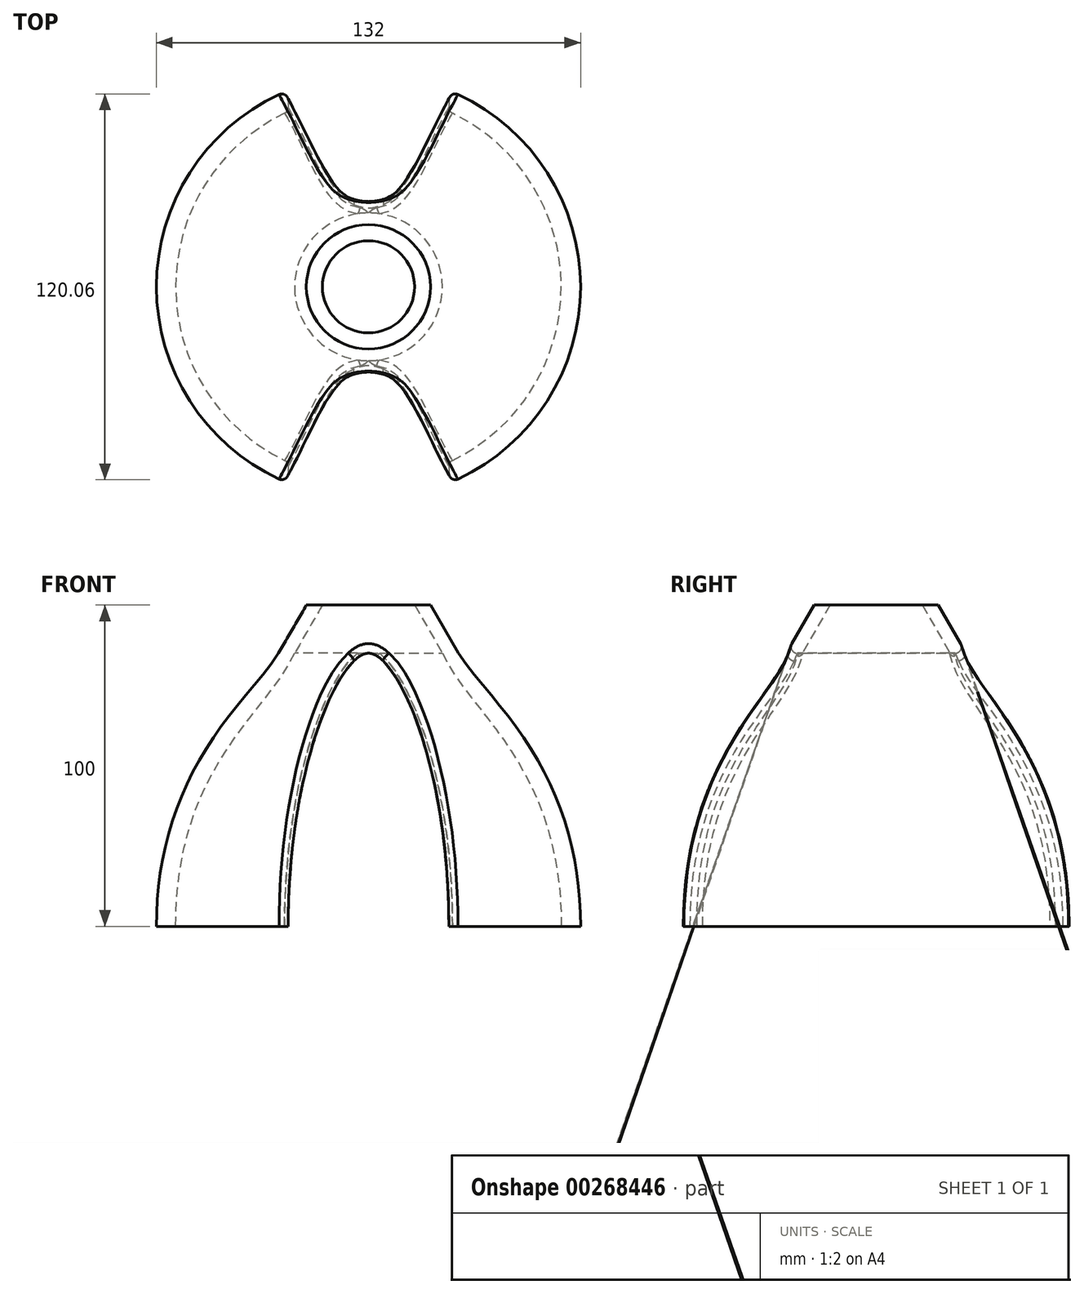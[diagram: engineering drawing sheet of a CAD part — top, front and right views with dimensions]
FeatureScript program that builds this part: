
annotation { "Feature Type Name" : "Feature", "Feature Type Description" : "" }
export const myFeature = defineFeature(function(context is Context, id is Id, definition is map)
    precondition{}
    {
        {
            var Q0;
            Q0=qCreatedBy(makeId("Front.planeOp"),FACE);
            var sketch = newSketch(context, id + "F0", { "sketchPlane" : qUnion([Q0])});
            skLineSegment(sketch, "E0", {"start": v(-14.34, 15) * mm, "end": v(-19.34, 15) * mm});
            skLineSegment(sketch, "E1", {"start": v(-19.34, 15) * mm, "end": v(-28, 0) * mm});
            skLineSegment(sketch, "E2", {"start": v(-28, 0) * mm, "end": v(-23, 0) * mm});
            skLineSegment(sketch, "E3.bottom", {"start": v(0, 0) * mm, "end": v(44.52, 0) * mm, "construction": true});
            skLineSegment(sketch, "E3.top", {"start": v(0, 38.4) * mm, "end": v(44.52, 38.4) * mm, "construction": true});
            skLineSegment(sketch, "E3.left", {"start": v(0, 0) * mm, "end": v(0, 38.4) * mm, "construction": true});
            skLineSegment(sketch, "E3.right", {"start": v(44.52, 0) * mm, "end": v(44.52, 38.4) * mm, "construction": true});
            skLineSegment(sketch, "E4", {"start": v(-14.34, 15) * mm, "end": v(-23, 0) * mm});
            skSolve(sketch);
        }
        {
            var Q0;
            Q0=makeQuery(id+"F0.imprint","IMPRINT",FACE,{"disambiguationData":[TD([[makeQuery(id+"F0.imprint","IMPRINT",EDGE,{"derivedFrom":sQuery(id+"F0.wireOp",EDGE,"E0")}),1.0]])]});
            var Q1;
            Q1=sQuery(id+"F0.wireOp",EDGE,"E3.left");
            revolve(context, id + "F1", {"surfaceOperationType" : NewSurfaceOperationType.NEW, "entities" : qUnion([Q0]), "axis" : qUnion([Q1]), "revolveType" : RevolveType.FULL});
        }
        {
            var Q0;
            Q0=qCreatedBy(makeId("Front.planeOp"),FACE);
            var sketch = newSketch(context, id + "F2", { "sketchPlane" : qUnion([Q0])});
            skLineSegment(sketch, "E5", {"start": v(-28, 0) * mm, "end": v(-19.38, 14.93) * mm, "construction": true});
            skFitSpline(sketch, "E6", {"points": [v(-28, 0) * mm, v(-66, -85) * mm], "startDerivative": vector(-22.5, -38.97) * mm, "endDerivative": vector(0, -150) * mm});
            skLineSegment(sketch, "E7", {"start": v(-66, -85) * mm, "end": v(-60, -85) * mm});
            skLineSegment(sketch, "E8.0", {"start": v(23, 0) * mm, "end": v(-23, 0) * mm, "construction": true});
            skFitSpline(sketch, "E9", {"points": [v(-60, -85) * mm, v(-23, 0) * mm], "startDerivative": vector(0, 150) * mm, "endDerivative": vector(25.12, 56.33) * mm});
            skLineSegment(sketch, "E10.0", {"start": v(14.34, 15) * mm, "end": v(-14.34, 15) * mm, "construction": true});
            skLineSegment(sketch, "E11", {"start": v(-14.34, 15) * mm, "end": v(-23, 0) * mm, "construction": true});
            skLineSegment(sketch, "E12", {"start": v(-28, 0) * mm, "end": v(-23, 0) * mm});
            skLineSegment(sketch, "E13", {"start": v(0, 0) * mm, "end": v(0, -38.45) * mm, "construction": true});
            skSolve(sketch);
        }
        {
            var Q0;
            Q0=makeQuery(id+"F2.imprint","IMPRINT",FACE,{"disambiguationData":[TD([[makeQuery(id+"F2.imprint","IMPRINT",EDGE,{"derivedFrom":sQuery(id+"F2.wireOp",EDGE,"E6")}),1.0]])]});
            var Q1;
            Q1=sQuery(id+"F2.wireOp",EDGE,"E13");
            revolve(context, id + "F3", {"operationType" : NewBodyOperationType.ADD, "surfaceOperationType" : NewSurfaceOperationType.NEW, "entities" : qUnion([Q0]), "axis" : qUnion([Q1]), "revolveType" : RevolveType.FULL});
        }
        {
            var Q0;
            Q0=qCreatedBy(makeId("Front.planeOp"),FACE);
            var sketch = newSketch(context, id + "F4", { "sketchPlane" : qUnion([Q0])});
            skLineSegment(sketch, "E14.0", {"start": v(-66, -85) * mm, "end": v(66, -85) * mm});
            skLineSegment(sketch, "E15", {"start": v(0, 0) * mm, "end": v(0, -85) * mm, "construction": true});
            skFitSpline(sketch, "E16", {"points": [v(0, 0) * mm, v(-25, -85) * mm], "startDerivative": vector(-26.97, 0) * mm, "endDerivative": vector(0, -150) * mm});
            skLineSegment(sketch, "E17", {"start": v(0, 0) * mm, "end": v(-8.99, 0) * mm, "construction": true});
            skFitSpline(sketch, "E18.MirrorCS", {"points": [v(0, 0) * mm, v(25, -85) * mm], "startDerivative": vector(26.97, 0) * mm, "endDerivative": vector(0, -150) * mm});
            skSolve(sketch);
        }
        {
            var Q0;
            {var subQ0=sQuery(id+"F4.wireOp",EDGE,"E16");Q0=makeQuery(id+"F4.imprint","IMPRINT",FACE,{"disambiguationData":[TD([[makeQuery(id+"F4.imprint","IMPRINT",EDGE,{"derivedFrom":subQ0}),1.0]])]});}
            extrude(context, id + "F5", {"entities" : qUnion([Q0]), "operationType" : NewBodyOperationType.REMOVE, "oppositeDirection" : true, "depth" : 200 * mm, "offsetDistance" : 25 * mm, "symmetric" : true});
        }
        {
            var Q0;
            Q0=makeQuery(id+"F5.boolean.opBoolean","INTERSECT",EDGE,{"disambiguationData":[OD(0.0)],"derivedFrom":[makeQuery(id+"F3.opRevolve","SWEPT_FACE",FACE,{"disambiguationData":[OSD([sQuery(id+"F2.wireOp",EDGE,"E6")])]}),makeQuery(id+"F5.opExtrude","SWEPT_FACE",FACE,{"disambiguationData":[OSD([sQuery(id+"F4.wireOp",EDGE,"E16")])]})]});
            var Q1;
            Q1=makeQuery(id+"F5.boolean.opBoolean","INTERSECT",EDGE,{"disambiguationData":[OD(0.0)],"derivedFrom":[makeQuery(id+"F3.opRevolve","SWEPT_FACE",FACE,{"disambiguationData":[OSD([sQuery(id+"F2.wireOp",EDGE,"E6")])]}),makeQuery(id+"F5.opExtrude","SWEPT_FACE",FACE,{"disambiguationData":[OSD([sQuery(id+"F4.wireOp",EDGE,"E18.MirrorCS")])]})]});
            var Q2;
            Q2=makeQuery(id+"FsHivhGLS4HPiXr_1.1.F5.boolean.opBoolean","INTERSECT",EDGE,{"derivedFrom":[makeQuery(id+"F5.boolean.opBoolean","SPLIT",FACE,{"disambiguationData":[OD(1.0)],"derivedFrom":makeQuery(id+"F3.opRevolve","SWEPT_FACE",FACE,{"disambiguationData":[OSD([sQuery(id+"F2.wireOp",EDGE,"E6")])]})}),makeQuery(id+"FsHivhGLS4HPiXr_1.1.F5.opExtrude","SWEPT_FACE",FACE,{"disambiguationData":[OSD([sQuery(id+"F4.wireOp",EDGE,"E16")])]})]});
            var Q3;
            Q3=makeQuery(id+"FsHivhGLS4HPiXr_1.1.F5.boolean.opBoolean","INTERSECT",EDGE,{"derivedFrom":[makeQuery(id+"F5.boolean.opBoolean","SPLIT",FACE,{"disambiguationData":[OD(1.0)],"derivedFrom":makeQuery(id+"F3.opRevolve","SWEPT_FACE",FACE,{"disambiguationData":[OSD([sQuery(id+"F2.wireOp",EDGE,"E6")])]})}),makeQuery(id+"FsHivhGLS4HPiXr_1.1.F5.opExtrude","SWEPT_FACE",FACE,{"disambiguationData":[OSD([sQuery(id+"F4.wireOp",EDGE,"E18.MirrorCS")])]})]});
            var Q4;
            {var subQ0=sQuery(id+"F4.wireOp",EDGE,"E16");var subQ1=makeQuery(id+"F3.opRevolve","SWEPT_FACE",FACE,{"disambiguationData":[OSD([sQuery(id+"F2.wireOp",EDGE,"E6")])]});Q4=makeQuery(id+"FsHivhGLS4HPiXr_1.2.F5.boolean.opBoolean","INTERSECT",EDGE,{"derivedFrom":[makeQuery(id+"FsHivhGLS4HPiXr_1.1.F5.boolean.opBoolean","SPLIT",FACE,{"disambiguationData":[TD([makeQuery(id+"F5.boolean.opBoolean","COPY",FACE,{"disambiguationData":[OD(1.0)],"derivedFrom":makeQuery(id+"F5.opExtrude","SWEPT_FACE",FACE,{"disambiguationData":[OSD([subQ0])]})})])],"derivedFrom":makeQuery(id+"F5.boolean.opBoolean","SPLIT",FACE,{"disambiguationData":[OD(1.0)],"derivedFrom":subQ1})}),makeQuery(id+"FsHivhGLS4HPiXr_1.2.F5.opExtrude","SWEPT_FACE",FACE,{"disambiguationData":[OSD([subQ0])]})]});}
            var Q5;
            Q5=makeQuery(id+"F5.boolean.opBoolean","INTERSECT",EDGE,{"disambiguationData":[OD(1.0)],"derivedFrom":[makeQuery(id+"F3.opRevolve","SWEPT_FACE",FACE,{"disambiguationData":[OSD([sQuery(id+"F2.wireOp",EDGE,"E6")])]}),makeQuery(id+"F5.opExtrude","SWEPT_FACE",FACE,{"disambiguationData":[OSD([sQuery(id+"F4.wireOp",EDGE,"E18.MirrorCS")])]})]});
            var Q6;
            Q6=makeQuery(id+"F5.boolean.opBoolean","INTERSECT",EDGE,{"disambiguationData":[OD(1.0)],"derivedFrom":[makeQuery(id+"F3.opRevolve","SWEPT_FACE",FACE,{"disambiguationData":[OSD([sQuery(id+"F2.wireOp",EDGE,"E6")])]}),makeQuery(id+"F5.opExtrude","SWEPT_FACE",FACE,{"disambiguationData":[OSD([sQuery(id+"F4.wireOp",EDGE,"E16")])]})]});
            var Q7;
            Q7=makeQuery(id+"FsHivhGLS4HPiXr_1.1.F5.boolean.opBoolean","INTERSECT",EDGE,{"derivedFrom":[makeQuery(id+"F5.boolean.opBoolean","SPLIT",FACE,{"disambiguationData":[OD(0.0)],"derivedFrom":makeQuery(id+"F3.opRevolve","SWEPT_FACE",FACE,{"disambiguationData":[OSD([sQuery(id+"F2.wireOp",EDGE,"E6")])]})}),makeQuery(id+"FsHivhGLS4HPiXr_1.1.F5.opExtrude","SWEPT_FACE",FACE,{"disambiguationData":[OSD([sQuery(id+"F4.wireOp",EDGE,"E16")])]})]});
            var Q8;
            Q8=makeQuery(id+"FsHivhGLS4HPiXr_1.1.F5.boolean.opBoolean","INTERSECT",EDGE,{"derivedFrom":[makeQuery(id+"F5.boolean.opBoolean","SPLIT",FACE,{"disambiguationData":[OD(0.0)],"derivedFrom":makeQuery(id+"F3.opRevolve","SWEPT_FACE",FACE,{"disambiguationData":[OSD([sQuery(id+"F2.wireOp",EDGE,"E6")])]})}),makeQuery(id+"FsHivhGLS4HPiXr_1.1.F5.opExtrude","SWEPT_FACE",FACE,{"disambiguationData":[OSD([sQuery(id+"F4.wireOp",EDGE,"E18.MirrorCS")])]})]});
            var Q9;
            {var subQ0=sQuery(id+"F4.wireOp",EDGE,"E18.MirrorCS");var subQ1=sQuery(id+"F4.wireOp",EDGE,"E16");var subQ2=makeQuery(id+"F3.opRevolve","SWEPT_FACE",FACE,{"disambiguationData":[OSD([sQuery(id+"F2.wireOp",EDGE,"E6")])]});Q9=makeQuery(id+"FsHivhGLS4HPiXr_1.2.F5.boolean.opBoolean","INTERSECT",EDGE,{"derivedFrom":[makeQuery(id+"FsHivhGLS4HPiXr_1.1.F5.boolean.opBoolean","SPLIT",FACE,{"disambiguationData":[TD([makeQuery(id+"F5.boolean.opBoolean","COPY",FACE,{"disambiguationData":[OD(0.0)],"derivedFrom":makeQuery(id+"F5.opExtrude","SWEPT_FACE",FACE,{"disambiguationData":[OSD([subQ1])]})})])],"derivedFrom":makeQuery(id+"F5.boolean.opBoolean","SPLIT",FACE,{"disambiguationData":[OD(0.0)],"derivedFrom":subQ2})}),makeQuery(id+"FsHivhGLS4HPiXr_1.2.F5.opExtrude","SWEPT_FACE",FACE,{"disambiguationData":[OSD([subQ0])]})]});}
            var Q10;
            {var subQ0=sQuery(id+"F4.wireOp",EDGE,"E16");var subQ1=makeQuery(id+"F3.opRevolve","SWEPT_FACE",FACE,{"disambiguationData":[OSD([sQuery(id+"F2.wireOp",EDGE,"E6")])]});Q10=makeQuery(id+"FsHivhGLS4HPiXr_1.2.F5.boolean.opBoolean","INTERSECT",EDGE,{"derivedFrom":[makeQuery(id+"FsHivhGLS4HPiXr_1.1.F5.boolean.opBoolean","SPLIT",FACE,{"disambiguationData":[TD([makeQuery(id+"F5.boolean.opBoolean","COPY",FACE,{"disambiguationData":[OD(0.0)],"derivedFrom":makeQuery(id+"F5.opExtrude","SWEPT_FACE",FACE,{"disambiguationData":[OSD([subQ0])]})})])],"derivedFrom":makeQuery(id+"F5.boolean.opBoolean","SPLIT",FACE,{"disambiguationData":[OD(0.0)],"derivedFrom":subQ1})}),makeQuery(id+"FsHivhGLS4HPiXr_1.2.F5.opExtrude","SWEPT_FACE",FACE,{"disambiguationData":[OSD([subQ0])]})]});}
            var Q11;
            {var subQ0=sQuery(id+"F4.wireOp",EDGE,"E18.MirrorCS");var subQ1=sQuery(id+"F4.wireOp",EDGE,"E16");var subQ2=makeQuery(id+"F3.opRevolve","SWEPT_FACE",FACE,{"disambiguationData":[OSD([sQuery(id+"F2.wireOp",EDGE,"E6")])]});Q11=makeQuery(id+"FsHivhGLS4HPiXr_1.2.F5.boolean.opBoolean","INTERSECT",EDGE,{"derivedFrom":[makeQuery(id+"FsHivhGLS4HPiXr_1.1.F5.boolean.opBoolean","SPLIT",FACE,{"disambiguationData":[TD([makeQuery(id+"F5.boolean.opBoolean","COPY",FACE,{"disambiguationData":[OD(1.0)],"derivedFrom":makeQuery(id+"F5.opExtrude","SWEPT_FACE",FACE,{"disambiguationData":[OSD([subQ1])]})})])],"derivedFrom":makeQuery(id+"F5.boolean.opBoolean","SPLIT",FACE,{"disambiguationData":[OD(1.0)],"derivedFrom":subQ2})}),makeQuery(id+"FsHivhGLS4HPiXr_1.2.F5.opExtrude","SWEPT_FACE",FACE,{"disambiguationData":[OSD([subQ0])]})]});}
            var Q12;
            {var subQ0=sQuery(id+"F4.wireOp",EDGE,"E18.MirrorCS");var subQ1=makeQuery(id+"F3.opRevolve","SWEPT_FACE",FACE,{"disambiguationData":[OSD([sQuery(id+"F2.wireOp",EDGE,"E9")])]});var subQ2=sQuery(id+"F4.wireOp",EDGE,"E16");Q12=makeQuery(id+"FsHivhGLS4HPiXr_1.2.F5.boolean.opBoolean","INTERSECT",EDGE,{"derivedFrom":[makeQuery(id+"FsHivhGLS4HPiXr_1.1.F5.boolean.opBoolean","SPLIT",FACE,{"disambiguationData":[TD([makeQuery(id+"F5.boolean.opBoolean","COPY",FACE,{"disambiguationData":[OD(0.0)],"derivedFrom":makeQuery(id+"F5.opExtrude","SWEPT_FACE",FACE,{"disambiguationData":[OSD([subQ2])]})})])],"derivedFrom":makeQuery(id+"F5.boolean.opBoolean","SPLIT",FACE,{"disambiguationData":[OD(0.0)],"derivedFrom":subQ1})}),makeQuery(id+"FsHivhGLS4HPiXr_1.2.F5.opExtrude","SWEPT_FACE",FACE,{"disambiguationData":[OSD([subQ0])]})]});}
            var Q13;
            {var subQ0=sQuery(id+"F4.wireOp",EDGE,"E16");var subQ1=makeQuery(id+"F3.opRevolve","SWEPT_FACE",FACE,{"disambiguationData":[OSD([sQuery(id+"F2.wireOp",EDGE,"E9")])]});Q13=makeQuery(id+"FsHivhGLS4HPiXr_1.2.F5.boolean.opBoolean","INTERSECT",EDGE,{"derivedFrom":[makeQuery(id+"FsHivhGLS4HPiXr_1.1.F5.boolean.opBoolean","SPLIT",FACE,{"disambiguationData":[TD([makeQuery(id+"F5.boolean.opBoolean","COPY",FACE,{"disambiguationData":[OD(0.0)],"derivedFrom":makeQuery(id+"F5.opExtrude","SWEPT_FACE",FACE,{"disambiguationData":[OSD([subQ0])]})})])],"derivedFrom":makeQuery(id+"F5.boolean.opBoolean","SPLIT",FACE,{"disambiguationData":[OD(0.0)],"derivedFrom":subQ1})}),makeQuery(id+"FsHivhGLS4HPiXr_1.2.F5.opExtrude","SWEPT_FACE",FACE,{"disambiguationData":[OSD([subQ0])]})]});}
            var Q14;
            Q14=makeQuery(id+"F5.boolean.opBoolean","INTERSECT",EDGE,{"disambiguationData":[OD(0.0)],"derivedFrom":[makeQuery(id+"F3.opRevolve","SWEPT_FACE",FACE,{"disambiguationData":[OSD([sQuery(id+"F2.wireOp",EDGE,"E9")])]}),makeQuery(id+"F5.opExtrude","SWEPT_FACE",FACE,{"disambiguationData":[OSD([sQuery(id+"F4.wireOp",EDGE,"E16")])]})]});
            var Q15;
            Q15=makeQuery(id+"F5.boolean.opBoolean","INTERSECT",EDGE,{"disambiguationData":[OD(0.0)],"derivedFrom":[makeQuery(id+"F3.opRevolve","SWEPT_FACE",FACE,{"disambiguationData":[OSD([sQuery(id+"F2.wireOp",EDGE,"E9")])]}),makeQuery(id+"F5.opExtrude","SWEPT_FACE",FACE,{"disambiguationData":[OSD([sQuery(id+"F4.wireOp",EDGE,"E18.MirrorCS")])]})]});
            var Q16;
            Q16=makeQuery(id+"FsHivhGLS4HPiXr_1.1.F5.boolean.opBoolean","INTERSECT",EDGE,{"derivedFrom":[makeQuery(id+"F5.boolean.opBoolean","SPLIT",FACE,{"disambiguationData":[OD(1.0)],"derivedFrom":makeQuery(id+"F3.opRevolve","SWEPT_FACE",FACE,{"disambiguationData":[OSD([sQuery(id+"F2.wireOp",EDGE,"E9")])]})}),makeQuery(id+"FsHivhGLS4HPiXr_1.1.F5.opExtrude","SWEPT_FACE",FACE,{"disambiguationData":[OSD([sQuery(id+"F4.wireOp",EDGE,"E18.MirrorCS")])]})]});
            var Q17;
            Q17=makeQuery(id+"FsHivhGLS4HPiXr_1.1.F5.boolean.opBoolean","INTERSECT",EDGE,{"derivedFrom":[makeQuery(id+"F5.boolean.opBoolean","SPLIT",FACE,{"disambiguationData":[OD(1.0)],"derivedFrom":makeQuery(id+"F3.opRevolve","SWEPT_FACE",FACE,{"disambiguationData":[OSD([sQuery(id+"F2.wireOp",EDGE,"E9")])]})}),makeQuery(id+"FsHivhGLS4HPiXr_1.1.F5.opExtrude","SWEPT_FACE",FACE,{"disambiguationData":[OSD([sQuery(id+"F4.wireOp",EDGE,"E16")])]})]});
            var Q18;
            {var subQ0=sQuery(id+"F4.wireOp",EDGE,"E16");var subQ1=makeQuery(id+"F3.opRevolve","SWEPT_FACE",FACE,{"disambiguationData":[OSD([sQuery(id+"F2.wireOp",EDGE,"E9")])]});Q18=makeQuery(id+"FsHivhGLS4HPiXr_1.2.F5.boolean.opBoolean","INTERSECT",EDGE,{"derivedFrom":[makeQuery(id+"FsHivhGLS4HPiXr_1.1.F5.boolean.opBoolean","SPLIT",FACE,{"disambiguationData":[TD([makeQuery(id+"F5.boolean.opBoolean","COPY",FACE,{"disambiguationData":[OD(1.0)],"derivedFrom":makeQuery(id+"F5.opExtrude","SWEPT_FACE",FACE,{"disambiguationData":[OSD([subQ0])]})})])],"derivedFrom":makeQuery(id+"F5.boolean.opBoolean","SPLIT",FACE,{"disambiguationData":[OD(1.0)],"derivedFrom":subQ1})}),makeQuery(id+"FsHivhGLS4HPiXr_1.2.F5.opExtrude","SWEPT_FACE",FACE,{"disambiguationData":[OSD([subQ0])]})]});}
            var Q19;
            {var subQ0=sQuery(id+"F4.wireOp",EDGE,"E18.MirrorCS");var subQ1=sQuery(id+"F4.wireOp",EDGE,"E16");var subQ2=makeQuery(id+"F3.opRevolve","SWEPT_FACE",FACE,{"disambiguationData":[OSD([sQuery(id+"F2.wireOp",EDGE,"E9")])]});Q19=makeQuery(id+"FsHivhGLS4HPiXr_1.2.F5.boolean.opBoolean","INTERSECT",EDGE,{"derivedFrom":[makeQuery(id+"FsHivhGLS4HPiXr_1.1.F5.boolean.opBoolean","SPLIT",FACE,{"disambiguationData":[TD([makeQuery(id+"F5.boolean.opBoolean","COPY",FACE,{"disambiguationData":[OD(1.0)],"derivedFrom":makeQuery(id+"F5.opExtrude","SWEPT_FACE",FACE,{"disambiguationData":[OSD([subQ1])]})})])],"derivedFrom":makeQuery(id+"F5.boolean.opBoolean","SPLIT",FACE,{"disambiguationData":[OD(1.0)],"derivedFrom":subQ2})}),makeQuery(id+"FsHivhGLS4HPiXr_1.2.F5.opExtrude","SWEPT_FACE",FACE,{"disambiguationData":[OSD([subQ0])]})]});}
            var Q20;
            Q20=makeQuery(id+"F5.boolean.opBoolean","INTERSECT",EDGE,{"disambiguationData":[OD(1.0)],"derivedFrom":[makeQuery(id+"F3.opRevolve","SWEPT_FACE",FACE,{"disambiguationData":[OSD([sQuery(id+"F2.wireOp",EDGE,"E9")])]}),makeQuery(id+"F5.opExtrude","SWEPT_FACE",FACE,{"disambiguationData":[OSD([sQuery(id+"F4.wireOp",EDGE,"E18.MirrorCS")])]})]});
            var Q21;
            Q21=makeQuery(id+"F5.boolean.opBoolean","INTERSECT",EDGE,{"disambiguationData":[OD(1.0)],"derivedFrom":[makeQuery(id+"F3.opRevolve","SWEPT_FACE",FACE,{"disambiguationData":[OSD([sQuery(id+"F2.wireOp",EDGE,"E9")])]}),makeQuery(id+"F5.opExtrude","SWEPT_FACE",FACE,{"disambiguationData":[OSD([sQuery(id+"F4.wireOp",EDGE,"E16")])]})]});
            var Q22;
            Q22=makeQuery(id+"FsHivhGLS4HPiXr_1.1.F5.boolean.opBoolean","INTERSECT",EDGE,{"derivedFrom":[makeQuery(id+"F5.boolean.opBoolean","SPLIT",FACE,{"disambiguationData":[OD(0.0)],"derivedFrom":makeQuery(id+"F3.opRevolve","SWEPT_FACE",FACE,{"disambiguationData":[OSD([sQuery(id+"F2.wireOp",EDGE,"E9")])]})}),makeQuery(id+"FsHivhGLS4HPiXr_1.1.F5.opExtrude","SWEPT_FACE",FACE,{"disambiguationData":[OSD([sQuery(id+"F4.wireOp",EDGE,"E16")])]})]});
            var Q23;
            Q23=makeQuery(id+"FsHivhGLS4HPiXr_1.1.F5.boolean.opBoolean","INTERSECT",EDGE,{"derivedFrom":[makeQuery(id+"F5.boolean.opBoolean","SPLIT",FACE,{"disambiguationData":[OD(0.0)],"derivedFrom":makeQuery(id+"F3.opRevolve","SWEPT_FACE",FACE,{"disambiguationData":[OSD([sQuery(id+"F2.wireOp",EDGE,"E9")])]})}),makeQuery(id+"FsHivhGLS4HPiXr_1.1.F5.opExtrude","SWEPT_FACE",FACE,{"disambiguationData":[OSD([sQuery(id+"F4.wireOp",EDGE,"E18.MirrorCS")])]})]});
            fillet(context, id + "F6", {"entities" : qUnion([Q0, Q1, Q2, Q3, Q4, Q5, Q6, Q7, Q8, Q9, Q10, Q11, Q12, Q13, Q14, Q15, Q16, Q17, Q18, Q19, Q20, Q21, Q22, Q23]), "tangentPropagation" : true, "radius" : 2 * mm, "defaultsChanged" : false, "vertexSettings" : [], "allowEdgeOverflow" : false});
        }
    });
